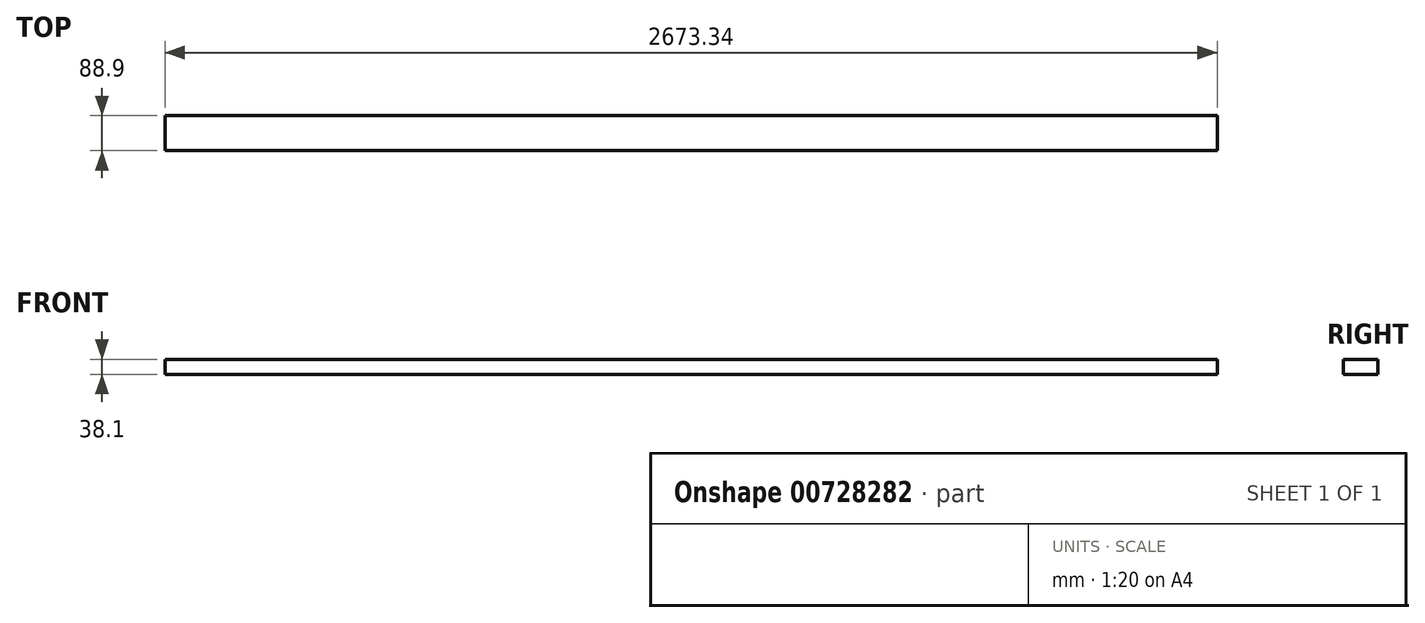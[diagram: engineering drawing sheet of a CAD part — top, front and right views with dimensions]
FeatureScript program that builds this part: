
annotation { "Feature Type Name" : "Feature", "Feature Type Description" : "" }
export const myFeature = defineFeature(function(context is Context, id is Id, definition is map)
    precondition{}
    {
        {
            var Q0;
            Q0=qCreatedBy(makeId("Top.planeOp"),FACE);
            var sketch = newSketch(context, id + "F0", { "sketchPlane" : qUnion([Q0])});
            skLineSegment(sketch, "E0.bottom", {"start": v(-1336.67, 44.45) * mm, "end": v(1336.67, 44.45) * mm});
            skLineSegment(sketch, "E0.top", {"start": v(-1336.67, -44.45) * mm, "end": v(1336.67, -44.45) * mm});
            skLineSegment(sketch, "E0.left", {"start": v(-1336.67, 44.45) * mm, "end": v(-1336.67, -44.45) * mm});
            skLineSegment(sketch, "E0.right", {"start": v(1336.67, 44.45) * mm, "end": v(1336.67, -44.45) * mm});
            skPoint(sketch, "E0.middle", {"position": v(0, 0) * mm});
            skSolve(sketch);
        }
        {
            var Q0;
            Q0=qSketchRegion(id+"F0",true);
            extrude(context, id + "F1", {"entities" : qUnion([Q0]), "depth" : 38.1 * mm, "offsetDistance" : 25.4 * mm});
        }
    });
